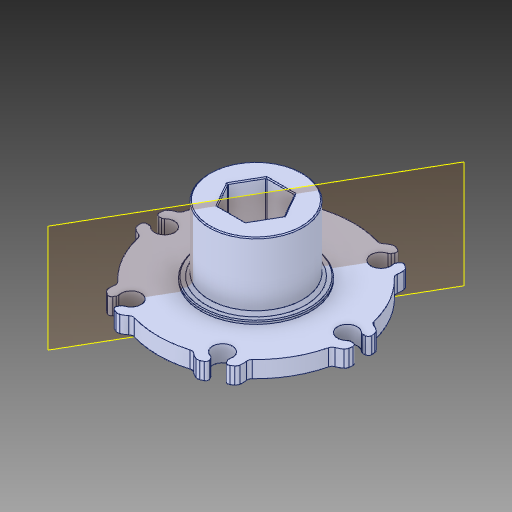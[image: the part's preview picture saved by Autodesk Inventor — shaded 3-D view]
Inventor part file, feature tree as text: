
AUTODESK INVENTOR PART (.ipt)
format: ipt  version: 2017.1 (Build 211199000, 199)  size: 352,256 bytes
history: native  units: in
note: dims shown in document units (in); Inventor stores cm internally (conversion verified against a paired STEP export)
features: plane x1, fillet x1
ambient origin geometry x8: Origin, YZ Plane, XZ Plane, XY Plane, X Axis, Y Axis, Z Axis, Center Point
bodies: Solid1 (feature_tree)
feature tree (2):
  plane  "Work Plane1"
  fillet  "Fillet7"  [1 undecoded]
note: 1 required parameter value undecoded (feature->parameter linkage not recoverable at this tier; creation-order binding heuristic only, values carry confidence <= 0.55)
